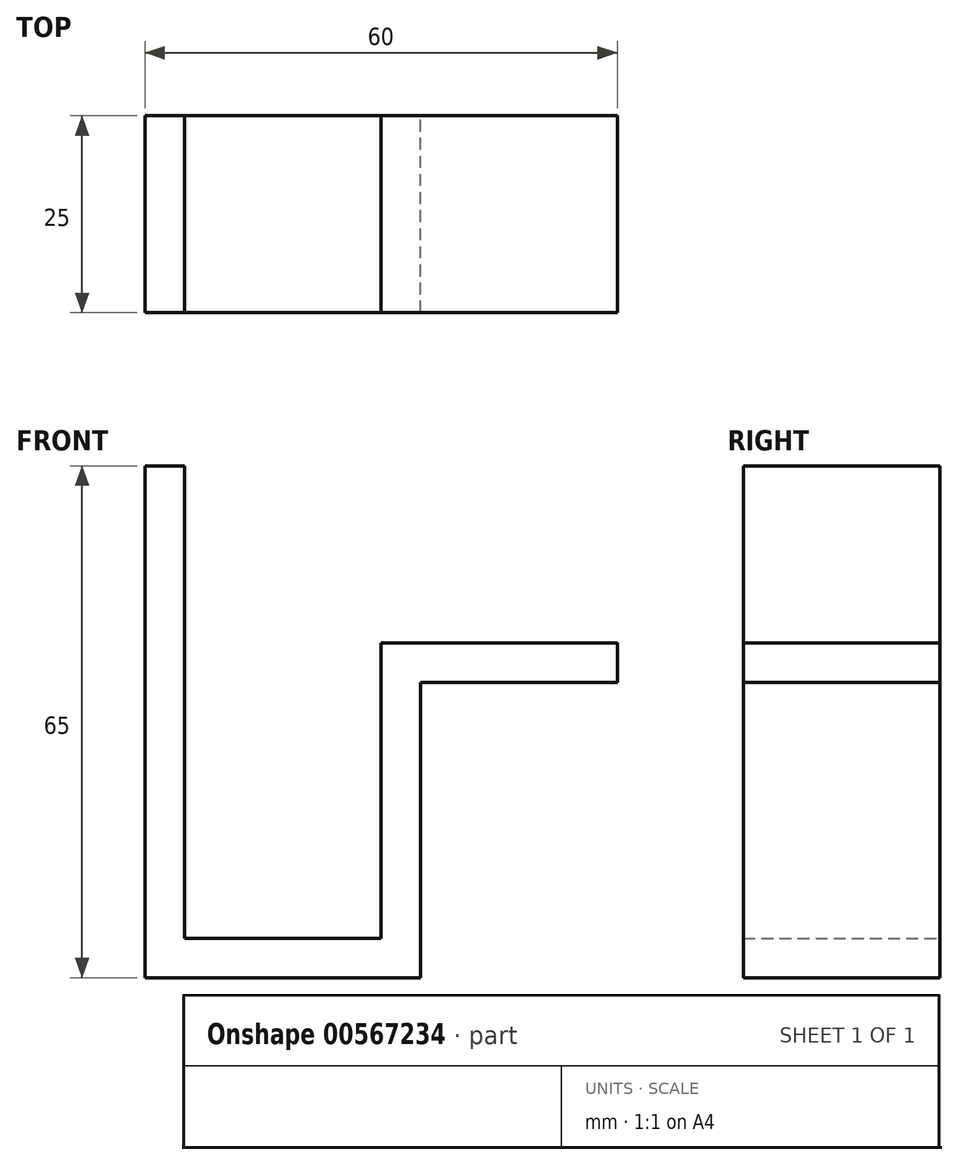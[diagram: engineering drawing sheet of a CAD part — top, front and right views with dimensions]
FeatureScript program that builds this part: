
annotation { "Feature Type Name" : "Feature", "Feature Type Description" : "" }
export const myFeature = defineFeature(function(context is Context, id is Id, definition is map)
    precondition{}
    {
        {
            var Q0;
            Q0=qCreatedBy(makeId("Front.planeOp"),FACE);
            var sketch = newSketch(context, id + "F0", { "sketchPlane" : qUnion([Q0])});
            skLineSegment(sketch, "E0", {"start": v(0, 60) * mm, "end": v(5, 60) * mm});
            skLineSegment(sketch, "E1", {"start": v(5, 60) * mm, "end": v(5, 0) * mm});
            skLineSegment(sketch, "E2", {"start": v(5, 0) * mm, "end": v(30, 0) * mm});
            skLineSegment(sketch, "E3", {"start": v(0, 60) * mm, "end": v(0, -5) * mm});
            skLineSegment(sketch, "E4", {"start": v(30, 0) * mm, "end": v(30, 37.5) * mm});
            skLineSegment(sketch, "E5", {"start": v(30, 37.5) * mm, "end": v(60, 37.5) * mm});
            skLineSegment(sketch, "E6", {"start": v(60, 37.5) * mm, "end": v(60, 32.5) * mm});
            skLineSegment(sketch, "E7", {"start": v(60, 32.5) * mm, "end": v(35, 32.5) * mm});
            skLineSegment(sketch, "E8", {"start": v(35, 32.5) * mm, "end": v(35, -5) * mm});
            skLineSegment(sketch, "E9", {"start": v(35, -5) * mm, "end": v(0, -5) * mm});
            skSolve(sketch);
        }
        {
            var Q0;
            Q0=makeQuery(id+"F0.imprint","IMPRINT",FACE,{"disambiguationData":[TD([[makeQuery(id+"F0.imprint","IMPRINT",EDGE,{"derivedFrom":sQuery(id+"F0.wireOp",EDGE,"E0")}),-1.0]])]});
            extrude(context, id + "F1", {"entities" : qUnion([Q0]), "depth" : 25 * mm, "offsetDistance" : 25 * mm});
        }
        {
            var Q0;
            Q0=makeQuery(id+"F1.opExtrude","SWEPT_FACE",FACE,{"disambiguationData":[OSD([sQuery(id+"F0.wireOp",EDGE,"E1")])]});
            var sketch = newSketch(context, id + "F2", { "sketchPlane" : qUnion([Q0])});
            skLineSegment(sketch, "E10", {"start": v(-12.5, 60) * mm, "end": v(-12.5, 30) * mm, "construction": true});
            skSolve(sketch);
        }
        {
            var Q0;
            Q0=makeQuery(id+"F1.opExtrude","SWEPT_FACE",FACE,{"disambiguationData":[OSD([sQuery(id+"F0.wireOp",EDGE,"E5")])]});
            var sketch = newSketch(context, id + "F3", { "sketchPlane" : qUnion([Q0])});
            skLineSegment(sketch, "E11", {"start": v(60, -12.5) * mm, "end": v(50, -12.5) * mm, "construction": true});
            skSolve(sketch);
        }
    });
